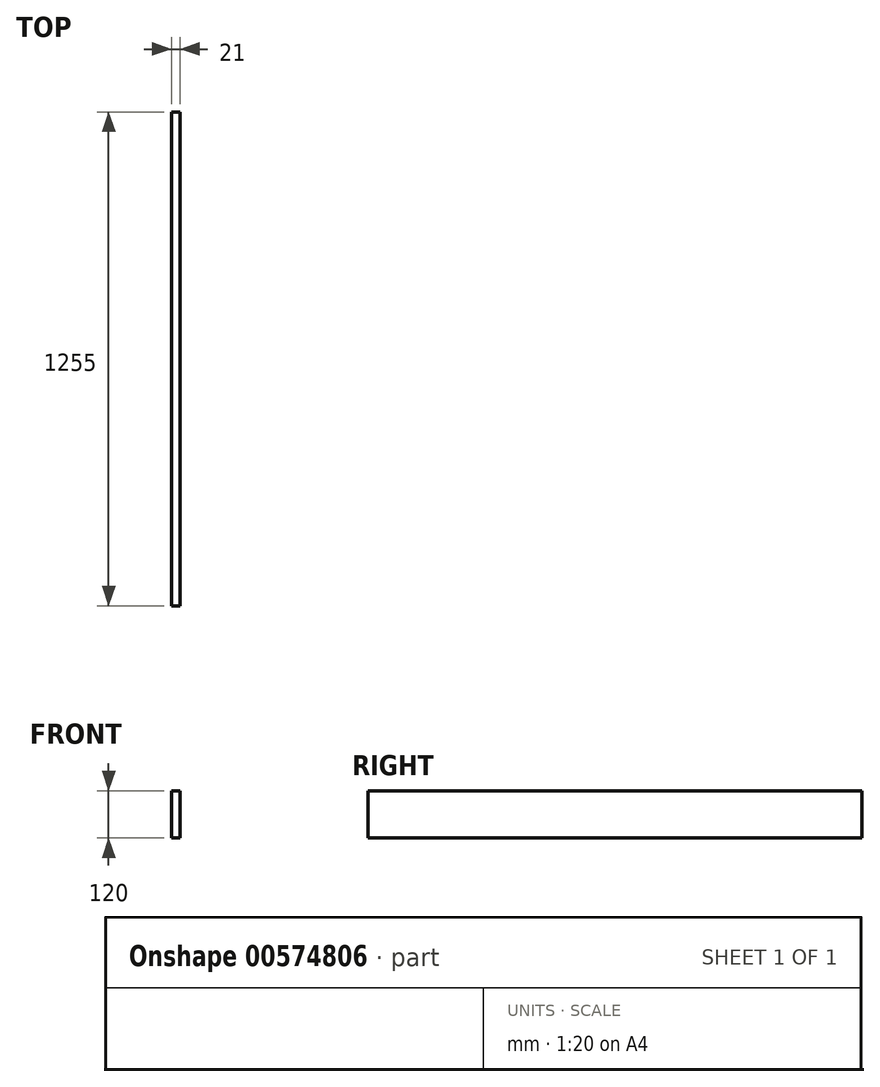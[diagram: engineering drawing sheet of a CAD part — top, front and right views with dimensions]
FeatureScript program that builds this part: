
annotation { "Feature Type Name" : "Feature", "Feature Type Description" : "" }
export const myFeature = defineFeature(function(context is Context, id is Id, definition is map)
    precondition{}
    {
        {
            var Q0;
            Q0=qCreatedBy(makeId("Front.planeOp"),FACE);
            var sketch = newSketch(context, id + "F0", { "sketchPlane" : qUnion([Q0])});
            skLineSegment(sketch, "E0.bottom", {"start": v(-10.5, 60) * mm, "end": v(10.5, 60) * mm});
            skLineSegment(sketch, "E0.top", {"start": v(-10.5, -60) * mm, "end": v(10.5, -60) * mm});
            skLineSegment(sketch, "E0.left", {"start": v(-10.5, 60) * mm, "end": v(-10.5, -60) * mm});
            skLineSegment(sketch, "E0.right", {"start": v(10.5, 60) * mm, "end": v(10.5, -60) * mm});
            skSolve(sketch);
        }
        {
            var Q0;
            Q0 = qSketchRegion(id + "F0", true);
            extrude(context, id + "F1", {"entities" : qUnion([Q0]), "depth" : 1255 * mm, "offsetDistance" : 25 * mm});
        }
    });
